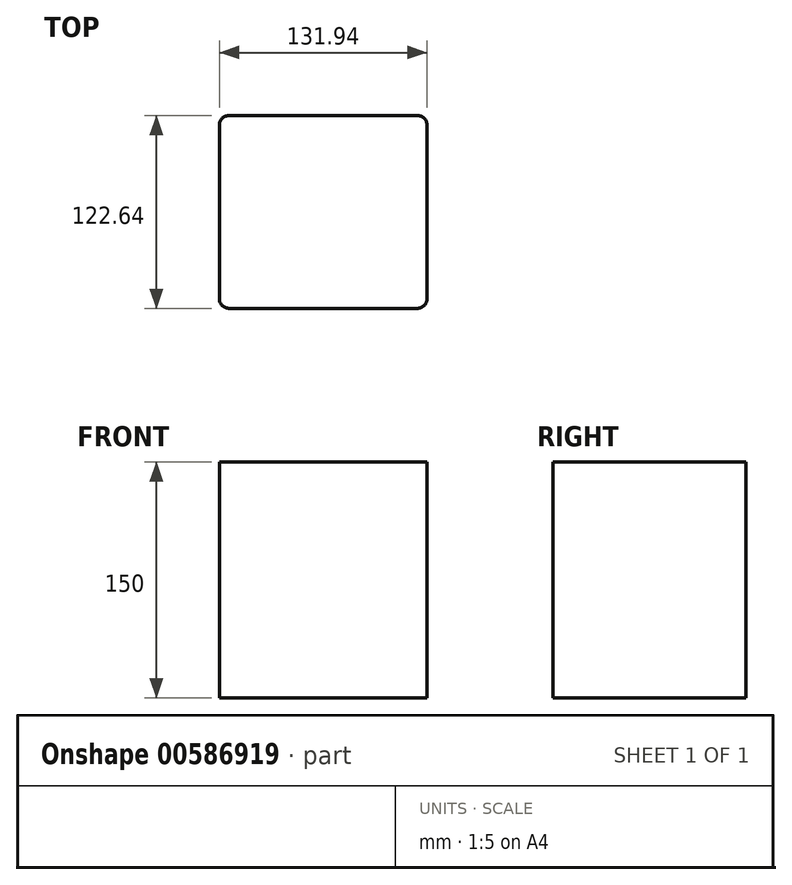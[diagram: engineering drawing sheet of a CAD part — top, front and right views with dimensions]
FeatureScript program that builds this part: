
annotation { "Feature Type Name" : "Feature", "Feature Type Description" : "" }
export const myFeature = defineFeature(function(context is Context, id is Id, definition is map)
    precondition{}
    {
        {
            var Q0;
            Q0=qCreatedBy(makeId("Top.planeOp"),FACE);
            var sketch = newSketch(context, id + "F0", { "sketchPlane" : qUnion([Q0])});
            skLineSegment(sketch, "E0.bottom", {"start": v(-59.62, -61.32) * mm, "end": v(59.62, -61.32) * mm});
            skLineSegment(sketch, "E0.top", {"start": v(-59.62, 61.32) * mm, "end": v(59.62, 61.32) * mm});
            skLineSegment(sketch, "E0.left", {"start": v(-65.97, -54.97) * mm, "end": v(-65.97, 54.97) * mm});
            skLineSegment(sketch, "E0.right", {"start": v(65.97, -54.97) * mm, "end": v(65.97, 54.97) * mm});
            skPoint(sketch, "E0.middle", {"position": v(0, 0) * mm});
            skPoint(sketch, "E1.visualSharp", {"position": v(-65.97, 61.32) * mm});
            skArc(sketch, "E1.filletArc", {"start": v(-59.62, 61.32) * mm, "mid": v(-64.11, 59.46) * mm, "end": v(-65.97, 54.97) * mm});
            skPoint(sketch, "E2.visualSharp", {"position": v(65.97, 61.32) * mm});
            skArc(sketch, "E2.filletArc", {"start": v(65.97, 54.97) * mm, "mid": v(64.11, 59.46) * mm, "end": v(59.62, 61.32) * mm});
            skPoint(sketch, "E3.visualSharp", {"position": v(65.97, -61.32) * mm});
            skArc(sketch, "E3.filletArc", {"start": v(59.62, -61.32) * mm, "mid": v(64.11, -59.46) * mm, "end": v(65.97, -54.97) * mm});
            skPoint(sketch, "E4.visualSharp", {"position": v(-65.97, -61.32) * mm});
            skArc(sketch, "E4.filletArc", {"start": v(-65.97, -54.97) * mm, "mid": v(-64.11, -59.46) * mm, "end": v(-59.62, -61.32) * mm});
            skSolve(sketch);
        }
        {
            var Q0;
            Q0 = qSketchRegion(id + "F0", true);
            extrude(context, id + "F1", {"entities" : qUnion([Q0]), "endBound" : BoundingType.SYMMETRIC, "depth" : 150 * mm, "offsetDistance" : 25.4 * mm});
        }
    });
